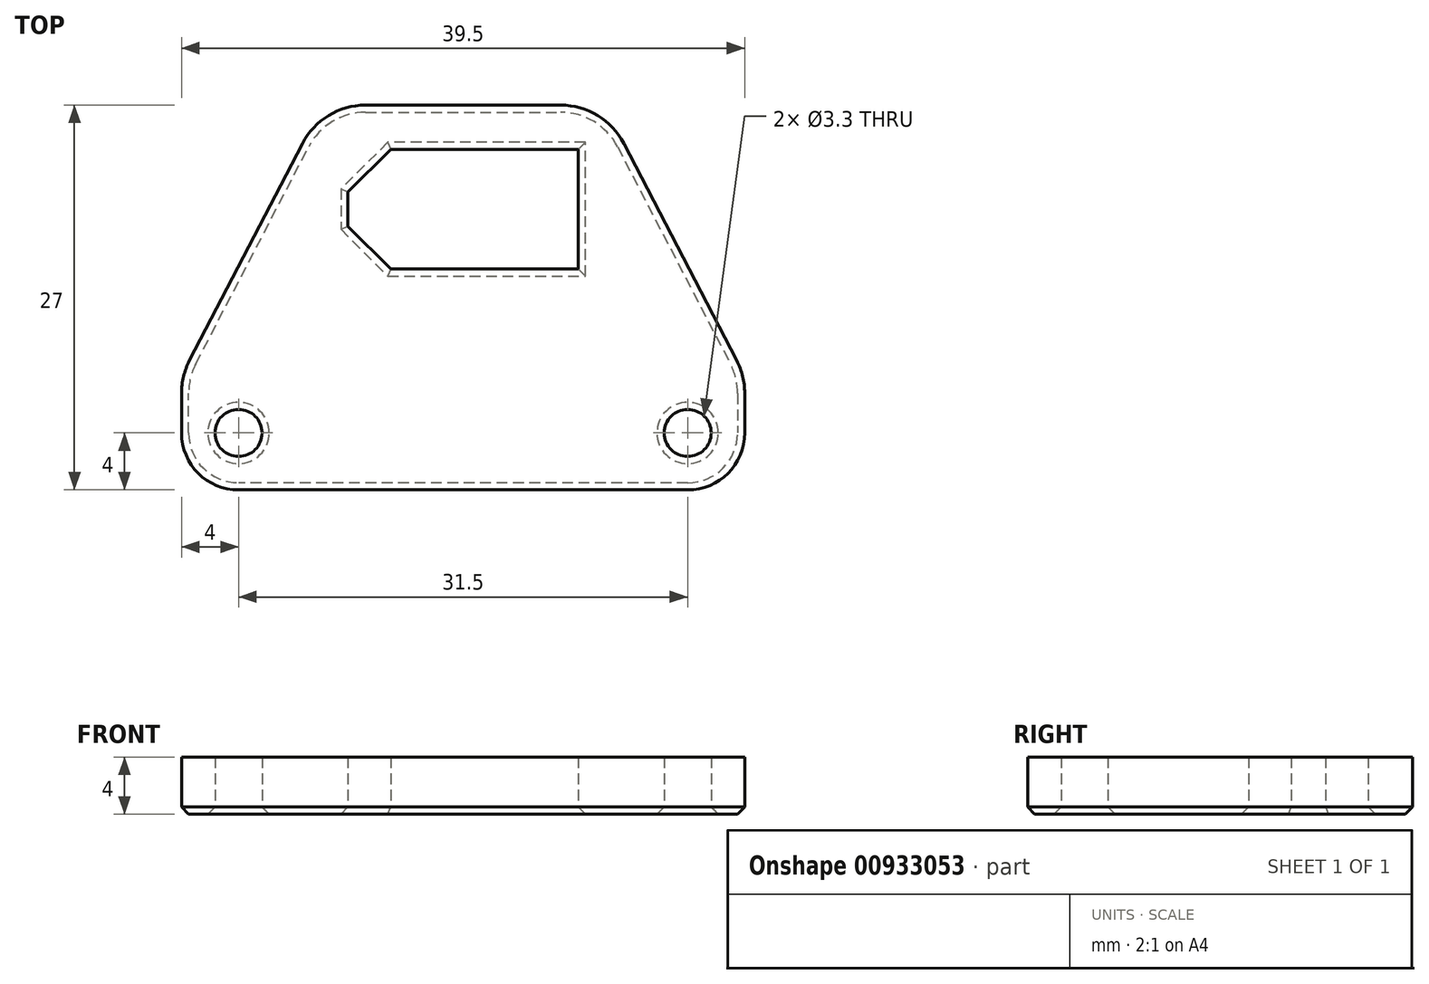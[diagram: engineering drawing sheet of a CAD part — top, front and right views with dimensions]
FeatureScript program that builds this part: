
annotation { "Feature Type Name" : "Feature", "Feature Type Description" : "" }
export const myFeature = defineFeature(function(context is Context, id is Id, definition is map)
    precondition{}
    {
        {
            var Q0;
            Q0=qCreatedBy(makeId("Top.planeOp"),FACE);
            var sketch = newSketch(context, id + "F0", { "sketchPlane" : qUnion([Q0])});
            skCircle(sketch, "E0", {"center": v(-15.75, 0) * mm, "radius": 1.65 * mm});
            skLineSegment(sketch, "E1", {"start": v(0, 0) * mm, "end": v(0, 23) * mm, "construction": true});
            skLineSegment(sketch, "E2", {"start": v(0, -4) * mm, "end": v(-19.75, -4) * mm});
            skLineSegment(sketch, "E3", {"start": v(-19.75, -4) * mm, "end": v(-19.75, 23) * mm});
            skLineSegment(sketch, "E4", {"start": v(-19.75, 23) * mm, "end": v(0, 23) * mm});
            skLineSegment(sketch, "E5.MirrorCS", {"start": v(19.75, 23) * mm, "end": v(0, 23) * mm});
            skLineSegment(sketch, "E6.MirrorCS", {"start": v(19.75, -4) * mm, "end": v(19.75, 23) * mm});
            skLineSegment(sketch, "E7.MirrorCS", {"start": v(0, -4) * mm, "end": v(19.75, -4) * mm});
            skCircle(sketch, "E8.MirrorC", {"center": v(15.75, 0) * mm, "radius": 1.65 * mm});
            skLineSegment(sketch, "E9", {"start": v(-8.08, 15.7) * mm, "end": v(-8.08, 16.9) * mm});
            skLineSegment(sketch, "E10", {"start": v(-8.08, 16.9) * mm, "end": v(-5.07, 19.9) * mm});
            skLineSegment(sketch, "E11", {"start": v(-5.07, 19.9) * mm, "end": v(8.08, 19.9) * mm});
            skLineSegment(sketch, "E12", {"start": v(8.08, 19.9) * mm, "end": v(8.08, 15.7) * mm});
            skLineSegment(sketch, "E13", {"start": v(-8.08, 15.7) * mm, "end": v(8.08, 15.7) * mm, "construction": true});
            skLineSegment(sketch, "E14.MirrorCS", {"start": v(8.08, 11.5) * mm, "end": v(8.08, 15.7) * mm});
            skLineSegment(sketch, "E15.MirrorCS", {"start": v(-8.08, 15.7) * mm, "end": v(-8.08, 14.5) * mm});
            skLineSegment(sketch, "E16.MirrorCS", {"start": v(-8.08, 14.5) * mm, "end": v(-5.07, 11.5) * mm});
            skLineSegment(sketch, "E17.MirrorCS", {"start": v(-5.07, 11.5) * mm, "end": v(8.08, 11.5) * mm});
            skLineSegment(sketch, "E18", {"start": v(8.08, 15.7) * mm, "end": v(19.75, 15.7) * mm, "construction": true});
            skLineSegment(sketch, "E19", {"start": v(-8.08, 15.7) * mm, "end": v(-19.75, 15.7) * mm, "construction": true});
            skLineSegment(sketch, "E20", {"start": v(-19.75, 4) * mm, "end": v(-9.87, 23) * mm});
            skLineSegment(sketch, "E21", {"start": v(19.75, 4) * mm, "end": v(9.87, 23) * mm});
            skSolve(sketch);
        }
        {
            var Q0;
            Q0=makeQuery(id+"F0.imprint","IMPRINT",FACE,{"disambiguationData":[TD([[makeQuery(id+"F0.imprint","IMPRINT",EDGE,{"derivedFrom":sQuery(id+"F0.wireOp",EDGE,"E0")}),-1.0]])]});
            extrude(context, id + "F1", {"entities" : qUnion([Q0]), "depth" : 4 * mm, "offsetDistance" : 25 * mm});
        }
        {
            var Q0;
            Q0=makeQuery(id+"F1.opExtrude","SWEPT_EDGE",EDGE,{"disambiguationData":[OSD([sQuery(id+"F0.wireOp",EDGE,"E3"),sQuery(id+"F0.wireOp",EDGE,"E20")])]});
            var Q1;
            Q1=makeQuery(id+"F1.opExtrude","SWEPT_EDGE",EDGE,{"disambiguationData":[OSD([sQuery(id+"F0.wireOp",EDGE,"E4"),sQuery(id+"F0.wireOp",EDGE,"E20")])]});
            var Q2;
            Q2=makeQuery(id+"F1.opExtrude","SWEPT_EDGE",EDGE,{"disambiguationData":[OSD([sQuery(id+"F0.wireOp",EDGE,"E5.MirrorCS"),sQuery(id+"F0.wireOp",EDGE,"E21")])]});
            var Q3;
            Q3=makeQuery(id+"F1.opExtrude","SWEPT_EDGE",EDGE,{"disambiguationData":[OSD([sQuery(id+"F0.wireOp",EDGE,"E6.MirrorCS"),sQuery(id+"F0.wireOp",EDGE,"E21")])]});
            fillet(context, id + "F2", {"entities" : qUnion([Q0, Q1, Q2, Q3]), "radius" : 5 * mm, "tangentPropagation" : true, "allowEdgeOverflow" : false});
        }
        {
            var Q0;
            Q0=makeQuery(id+"F1.opExtrude","SWEPT_EDGE",EDGE,{"disambiguationData":[OSD([sQuery(id+"F0.wireOp",EDGE,"E6.MirrorCS"),sQuery(id+"F0.wireOp",EDGE,"E7.MirrorCS")])]});
            var Q1;
            Q1=makeQuery(id+"F1.opExtrude","SWEPT_EDGE",EDGE,{"disambiguationData":[OSD([sQuery(id+"F0.wireOp",EDGE,"E2"),sQuery(id+"F0.wireOp",EDGE,"E3")])]});
            fillet(context, id + "F3", {"entities" : qUnion([Q0, Q1]), "radius" : 4 * mm, "tangentPropagation" : true, "allowEdgeOverflow" : false});
        }
        {
            var Q0;
            Q0=makeQuery(id+"F1.opExtrude","CAP_FACE",FACE,{"disambiguationData":[OSD([sQuery(id+"F0.wireOp",EDGE,"E0"),sQuery(id+"F0.wireOp",EDGE,"E2"),sQuery(id+"F0.wireOp",EDGE,"E3"),sQuery(id+"F0.wireOp",EDGE,"E4"),sQuery(id+"F0.wireOp",EDGE,"E5.MirrorCS"),sQuery(id+"F0.wireOp",EDGE,"E6.MirrorCS"),sQuery(id+"F0.wireOp",EDGE,"E7.MirrorCS"),sQuery(id+"F0.wireOp",EDGE,"E8.MirrorC"),sQuery(id+"F0.wireOp",EDGE,"E9"),sQuery(id+"F0.wireOp",EDGE,"E10"),sQuery(id+"F0.wireOp",EDGE,"E11"),sQuery(id+"F0.wireOp",EDGE,"E12"),sQuery(id+"F0.wireOp",EDGE,"E14.MirrorCS"),sQuery(id+"F0.wireOp",EDGE,"E15.MirrorCS"),sQuery(id+"F0.wireOp",EDGE,"E16.MirrorCS"),sQuery(id+"F0.wireOp",EDGE,"E17.MirrorCS")])],"isStart":true});
            chamfer(context, id + "F4", {"entities" : qUnion([Q0]), "width" : 0.5 * mm, "tangentPropagation" : true});
        }
    });
